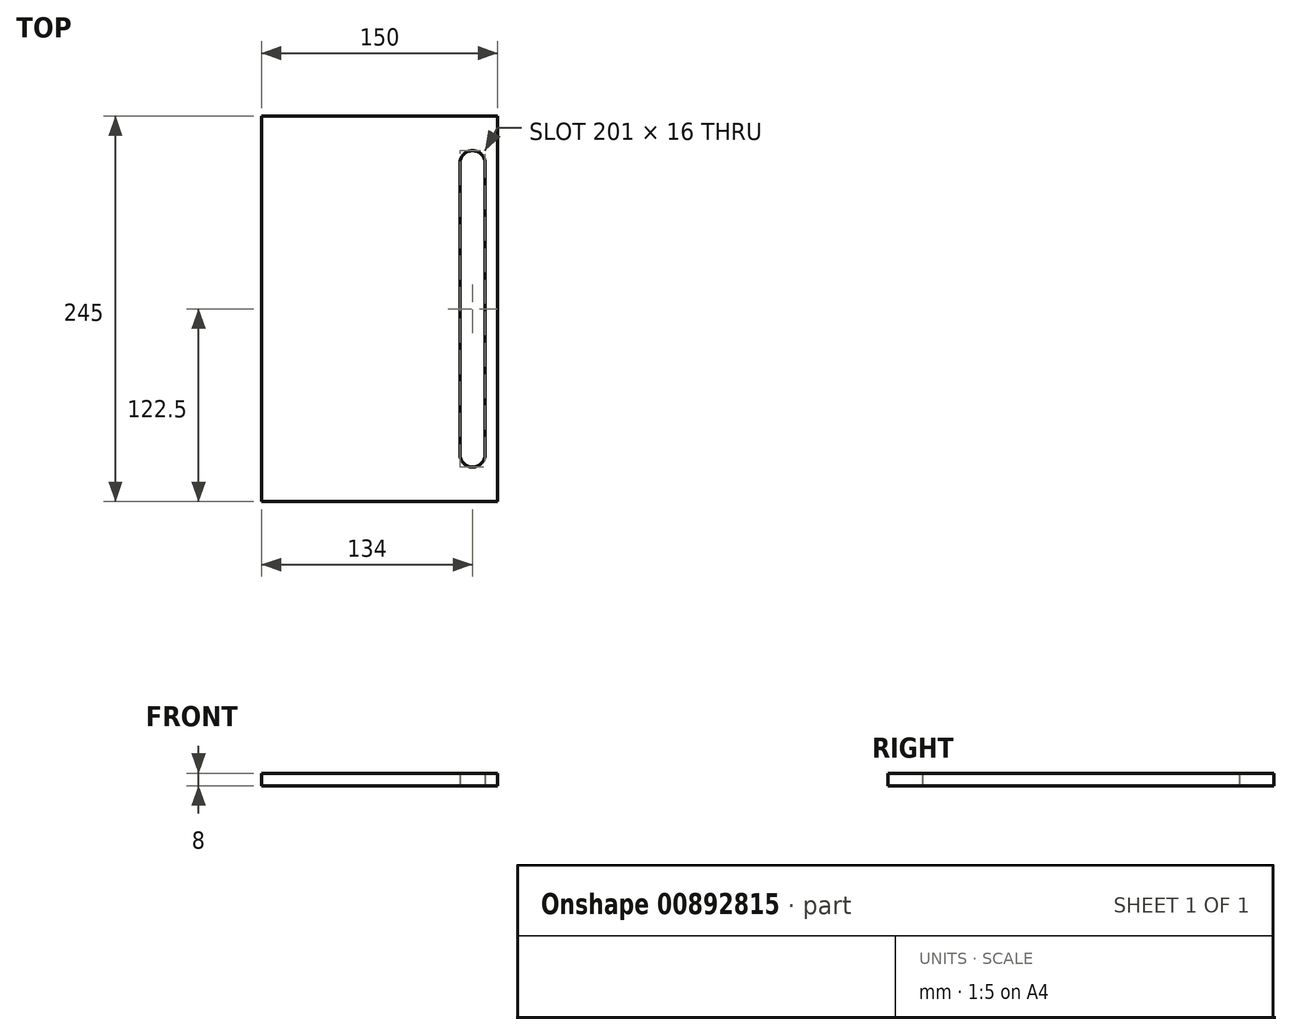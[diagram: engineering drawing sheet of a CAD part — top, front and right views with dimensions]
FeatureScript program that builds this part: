
annotation { "Feature Type Name" : "Feature", "Feature Type Description" : "" }
export const myFeature = defineFeature(function(context is Context, id is Id, definition is map)
    precondition{}
    {
        {
            var Q0;
            Q0=qCreatedBy(makeId("Top.planeOp"),FACE);
            var sketch = newSketch(context, id + "F0", { "sketchPlane" : qUnion([Q0])});
            skLineSegment(sketch, "E0.bottom", {"start": v(-75, 122.5) * mm, "end": v(75, 122.5) * mm});
            skLineSegment(sketch, "E0.top", {"start": v(-75, -122.5) * mm, "end": v(75, -122.5) * mm});
            skLineSegment(sketch, "E0.left", {"start": v(-75, 122.5) * mm, "end": v(-75, -122.5) * mm});
            skLineSegment(sketch, "E0.right", {"start": v(75, 122.5) * mm, "end": v(75, -122.5) * mm});
            skPoint(sketch, "E0.middle", {"position": v(0, 0) * mm});
            skLineSegment(sketch, "E1", {"start": v(59, 92.5) * mm, "end": v(59, -92.5) * mm, "construction": true});
            skArc(sketch, "E2.0.startCap", {"start": v(51, 92.5) * mm, "mid": v(59, 100.5) * mm, "end": v(67, 92.5) * mm});
            skArc(sketch, "E2.0.endCap", {"start": v(67, -92.5) * mm, "mid": v(59, -100.5) * mm, "end": v(51, -92.5) * mm});
            skLineSegment(sketch, "E2.0.left", {"start": v(67, 92.5) * mm, "end": v(67, -92.5) * mm});
            skLineSegment(sketch, "E2.0.right", {"start": v(51, 92.5) * mm, "end": v(51, -92.5) * mm});
            skSolve(sketch);
        }
        {
            var Q0;
            Q0=makeQuery(id+"F0.imprint","IMPRINT",FACE,{"disambiguationData":[TD([[makeQuery(id+"F0.imprint","IMPRINT",EDGE,{"derivedFrom":sQuery(id+"F0.wireOp",EDGE,"E0.bottom")}),-1.0]])]});
            extrude(context, id + "F1", {"entities" : qUnion([Q0]), "depth" : 8 * mm, "offsetDistance" : 25 * mm});
        }
    });
